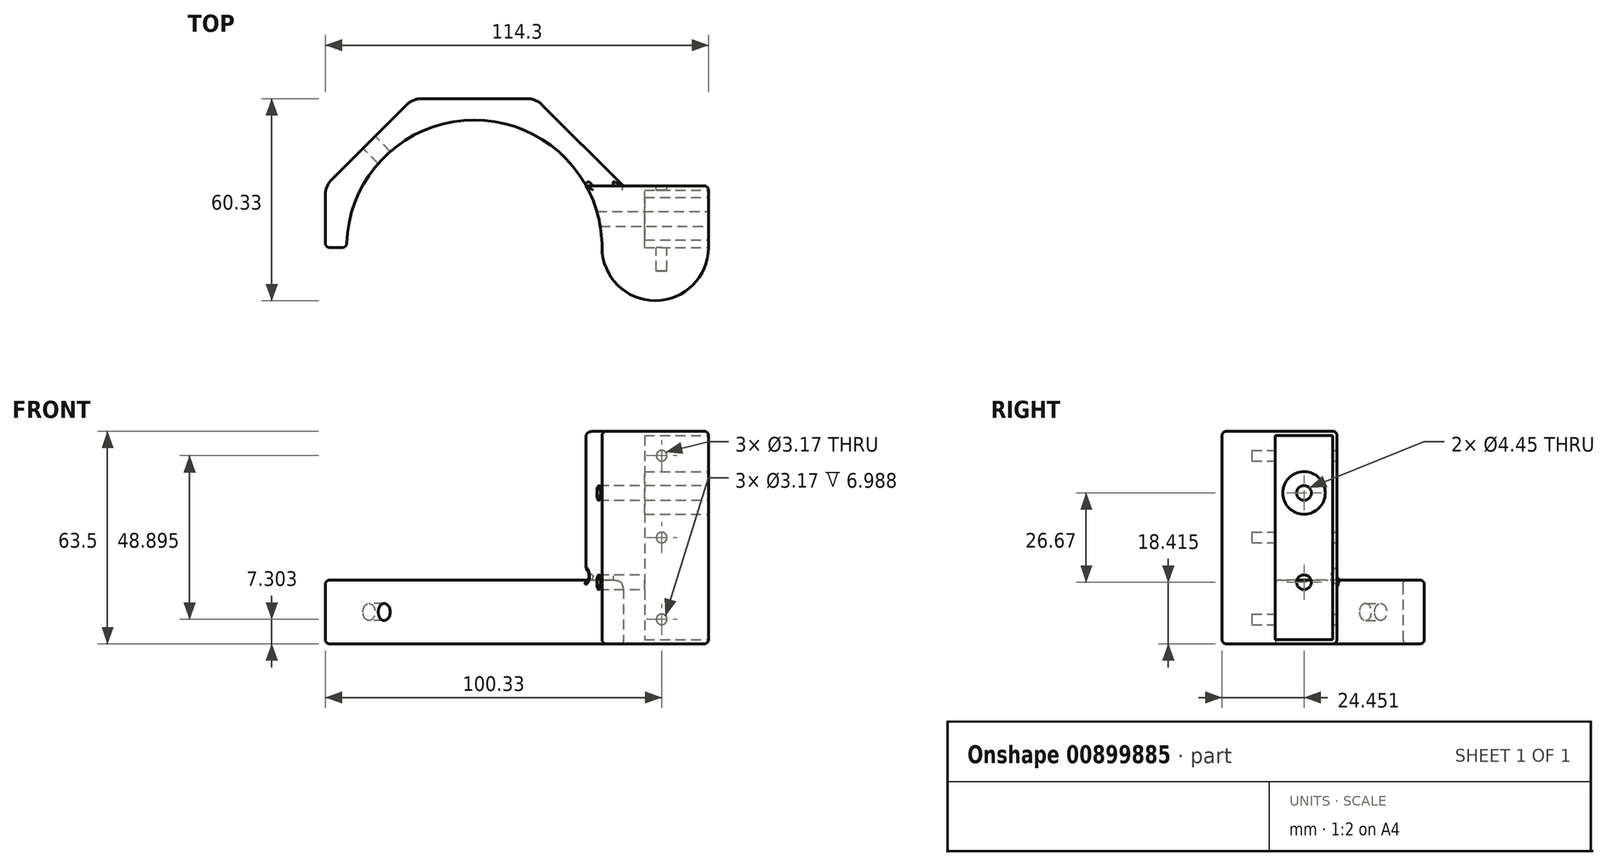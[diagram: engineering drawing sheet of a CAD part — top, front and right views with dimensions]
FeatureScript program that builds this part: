
annotation { "Feature Type Name" : "Feature", "Feature Type Description" : "" }
export const myFeature = defineFeature(function(context is Context, id is Id, definition is map)
    precondition{}
    {
        {
            var Q0;
            Q0=qCreatedBy(makeId("Top.planeOp"),FACE);
            var sketch = newSketch(context, id + "F0", { "sketchPlane" : qUnion([Q0])});
            skArc(sketch, "E0", {"start": v(38.1, 0) * mm, "mid": v(0, 38.1) * mm, "end": v(-38.1, 0) * mm});
            skCircle(sketch, "E1.cCircle", {"center": v(0, 0) * mm, "radius": 44.45 * mm, "construction": true});
            skLineSegment(sketch, "E1.0", {"start": v(44.45, 18.41) * mm, "end": v(44.45, 0) * mm});
            skLineSegment(sketch, "E1.4", {"start": v(-44.45, 0) * mm, "end": v(-44.45, 18.41) * mm});
            skLineSegment(sketch, "E1.5", {"start": v(-44.45, 18.41) * mm, "end": v(-18.41, 44.45) * mm});
            skLineSegment(sketch, "E1.6", {"start": v(-18.41, 44.45) * mm, "end": v(18.41, 44.45) * mm});
            skLineSegment(sketch, "E1.7", {"start": v(18.41, 44.45) * mm, "end": v(44.45, 18.41) * mm});
            skPoint(sketch, "E1.0.midPoint", {"position": v(44.45, 0) * mm});
            skLineSegment(sketch, "E2", {"start": v(-44.45, 0) * mm, "end": v(-38.1, 0) * mm});
            skPoint(sketch, "E3.orphan", {"position": v(-44.45, -18.41) * mm});
            skPoint(sketch, "E4.orphan", {"position": v(44.45, -18.41) * mm});
            skLineSegment(sketch, "E5.trimOffspring", {"start": v(38.1, 0) * mm, "end": v(44.45, 0) * mm});
            skLineSegment(sketch, "E6", {"start": v(44.45, 0) * mm, "end": v(69.85, 0) * mm});
            skLineSegment(sketch, "E7", {"start": v(69.85, 0) * mm, "end": v(69.85, 18.41) * mm});
            skLineSegment(sketch, "E8", {"start": v(69.85, 18.41) * mm, "end": v(44.45, 18.41) * mm});
            skArc(sketch, "E9", {"start": v(38.1, 0) * mm, "mid": v(53.98, -15.88) * mm, "end": v(69.85, 0) * mm});
            skLineSegment(sketch, "E10", {"start": v(44.45, 18.41) * mm, "end": v(33.36, 18.41) * mm});
            skSolve(sketch);
        }
        {
            var Q0;
            Q0=makeQuery(id+"F0.imprint","IMPRINT",FACE,{"disambiguationData":[TD([[makeQuery(id+"F0.imprint","IMPRINT",EDGE,{"derivedFrom":sQuery(id+"F0.wireOp",EDGE,"E1.0")}),1.0]])]});
            var Q1;
            Q1=makeQuery(id+"F0.imprint","IMPRINT",FACE,{"disambiguationData":[TD([[makeQuery(id+"F0.imprint","IMPRINT",EDGE,{"derivedFrom":sQuery(id+"F0.wireOp",EDGE,"E5.trimOffspring")}),-1.0]])]});
            var Q2;
            Q2=makeQuery(id+"F0.imprint","IMPRINT",FACE,{"disambiguationData":[TD([[makeQuery(id+"F0.imprint","IMPRINT",EDGE,{"derivedFrom":sQuery(id+"F0.wireOp",EDGE,"E1.0")}),-1.0]])]});
            extrude(context, id + "F1", {"entities" : qUnion([Q0, Q1, Q2]), "depth" : 63.5 * mm, "offsetDistance" : 25.4 * mm});
        }
        {
            var Q0;
            Q0=makeQuery(id+"F0.imprint","IMPRINT",FACE,{"disambiguationData":[TD([[makeQuery(id+"F0.imprint","IMPRINT",EDGE,{"derivedFrom":sQuery(id+"F0.wireOp",EDGE,"E1.4")}),-1.0]])]});
            extrude(context, id + "F2", {"entities" : qUnion([Q0]), "operationType" : NewBodyOperationType.ADD, "depth" : 19.05 * mm, "offsetDistance" : 25.4 * mm});
        }
        {
            var Q0;
            Q0=makeQuery(id+"F2.opExtrude","SWEPT_EDGE",EDGE,{"disambiguationData":[OSD([sQuery(id+"F0.wireOp",EDGE,"E1.0"),sQuery(id+"F0.wireOp",EDGE,"E1.7"),sQuery(id+"F0.wireOp",EDGE,"E8"),sQuery(id+"F0.wireOp",EDGE,"E10")])]});
            var Q1;
            Q1=makeQuery(id+"F2.opExtrude","SWEPT_EDGE",EDGE,{"disambiguationData":[OSD([sQuery(id+"F0.wireOp",EDGE,"E1.6"),sQuery(id+"F0.wireOp",EDGE,"E1.7")])]});
            var Q2;
            Q2=makeQuery(id+"F2.opExtrude","SWEPT_EDGE",EDGE,{"disambiguationData":[OSD([sQuery(id+"F0.wireOp",EDGE,"E1.5"),sQuery(id+"F0.wireOp",EDGE,"E1.6")])]});
            var Q3;
            Q3=makeQuery(id+"F2.opExtrude","SWEPT_EDGE",EDGE,{"disambiguationData":[OSD([sQuery(id+"F0.wireOp",EDGE,"E1.4"),sQuery(id+"F0.wireOp",EDGE,"E1.5")])]});
            var Q4;
            Q4=makeQuery(id+"F2.opExtrude","CAP_EDGE",EDGE,{"disambiguationData":[OSD([sQuery(id+"F0.wireOp",EDGE,"E10")])],"isStart":false});
            fillet(context, id + "F3", {"entities" : qUnion([Q0, Q1, Q2, Q3, Q4]), "radius" : 6.35 * mm, "tangentPropagation" : true, "allowEdgeOverflow" : false});
        }
        {
            var Q0;
            Q0=makeQuery(id+"F1.opExtrude","SWEPT_EDGE",EDGE,{"disambiguationData":[OSD([sQuery(id+"F0.wireOp",EDGE,"E7"),sQuery(id+"F0.wireOp",EDGE,"E8")])]});
            var Q1;
            {var subQ0=sQuery(id+"F0.wireOp",EDGE,"E10");var subQ1=sQuery(id+"F0.wireOp",EDGE,"E0");Q1=makeQuery(id+"F2.boolean.opBoolean","MERGE",FACE,{"derivedFrom":[makeQuery(id+"F1.opExtrude","CAP_FACE",FACE,{"disambiguationData":[OSD([subQ1,sQuery(id+"F0.wireOp",EDGE,"E7"),sQuery(id+"F0.wireOp",EDGE,"E8"),sQuery(id+"F0.wireOp",EDGE,"E9"),subQ0])],"isStart":true}),makeQuery(id+"F2.opExtrude","CAP_FACE",FACE,{"disambiguationData":[OSD([subQ1,sQuery(id+"F0.wireOp",EDGE,"E1.4"),sQuery(id+"F0.wireOp",EDGE,"E1.5"),sQuery(id+"F0.wireOp",EDGE,"E1.6"),sQuery(id+"F0.wireOp",EDGE,"E1.7"),sQuery(id+"F0.wireOp",EDGE,"E2"),subQ0])],"isStart":true})]});}
            var Q2;
            Q2=makeQuery(id+"F2.opExtrude","SWEPT_FACE",FACE,{"disambiguationData":[OSD([sQuery(id+"F0.wireOp",EDGE,"E2")])]});
            var Q3;
            Q3=makeQuery(id+"F2.opExtrude","CAP_FACE",FACE,{"disambiguationData":[OSD([sQuery(id+"F0.wireOp",EDGE,"E0"),sQuery(id+"F0.wireOp",EDGE,"E1.4"),sQuery(id+"F0.wireOp",EDGE,"E1.5"),sQuery(id+"F0.wireOp",EDGE,"E1.6"),sQuery(id+"F0.wireOp",EDGE,"E1.7"),sQuery(id+"F0.wireOp",EDGE,"E2"),sQuery(id+"F0.wireOp",EDGE,"E10")])],"isStart":false});
            var Q4;
            Q4=makeQuery(id+"F1.opExtrude","CAP_FACE",FACE,{"disambiguationData":[OSD([sQuery(id+"F0.wireOp",EDGE,"E0"),sQuery(id+"F0.wireOp",EDGE,"E7"),sQuery(id+"F0.wireOp",EDGE,"E8"),sQuery(id+"F0.wireOp",EDGE,"E9"),sQuery(id+"F0.wireOp",EDGE,"E10")])],"isStart":false});
            fillet(context, id + "F4", {"entities" : qUnion([Q0, Q1, Q2, Q3, Q4]), "radius" : 1.27 * mm, "tangentPropagation" : true, "allowEdgeOverflow" : false});
        }
        {
            var Q0;
            Q0=makeQuery(id+"F2.opExtrude","SWEPT_FACE",FACE,{"disambiguationData":[OSD([sQuery(id+"F0.wireOp",EDGE,"E1.5")])]});
            var sketch = newSketch(context, id + "F5", { "sketchPlane" : qUnion([Q0])});
            skLineSegment(sketch, "E11", {"start": v(15.78, 1.27) * mm, "end": v(-15.78, 17.78) * mm});
            skCircle(sketch, "E12", {"center": v(0, 9.53) * mm, "radius": 2.54 * mm});
            skSolve(sketch);
        }
        {
            var Q0;
            {var subQ0=sQuery(id+"F5.wireOp",EDGE,"E12");var subQ1=sQuery(id+"F5.wireOp",EDGE,"E11");var subQ2=makeQuery(id+"F5.imprint","INTERSECT",VERTEX,{"disambiguationData":[OD(0.0)],"derivedFrom":[subQ1,subQ0]});Q0=makeQuery(id+"F5.imprint","IMPRINT",FACE,{"disambiguationData":[TD([[makeQuery(id+"F5.imprint","IMPRINT",EDGE,{"disambiguationData":[TD([[subQ2,-1.0]])],"derivedFrom":subQ1}),-1.0]])]});}
            var Q1;
            {var subQ0=sQuery(id+"F5.wireOp",EDGE,"E12");var subQ1=sQuery(id+"F5.wireOp",EDGE,"E11");var subQ2=makeQuery(id+"F5.imprint","INTERSECT",VERTEX,{"disambiguationData":[OD(0.0)],"derivedFrom":[subQ1,subQ0]});Q1=makeQuery(id+"F5.imprint","IMPRINT",FACE,{"disambiguationData":[TD([[makeQuery(id+"F5.imprint","IMPRINT",EDGE,{"disambiguationData":[TD([[subQ2,-1.0]])],"derivedFrom":subQ1}),1.0]])]});}
            extrude(context, id + "F6", {"entities" : qUnion([Q0, Q1]), "operationType" : NewBodyOperationType.REMOVE, "oppositeDirection" : true, "depth" : 25.4 * mm, "offsetDistance" : 25.4 * mm});
        }
        {
            var Q0;
            Q0=makeQuery(id+"F1.opExtrude","SWEPT_FACE",FACE,{"disambiguationData":[OSD([sQuery(id+"F0.wireOp",EDGE,"E8"),sQuery(id+"F0.wireOp",EDGE,"E10")])]});
            var sketch = newSketch(context, id + "F7", { "sketchPlane" : qUnion([Q0])});
            skLineSegment(sketch, "E13", {"start": v(-68.58, 56.2) * mm, "end": v(-68.58, 7.3) * mm});
            skLineSegment(sketch, "E14.0", {"start": v(-55.88, 56.2) * mm, "end": v(-55.88, 7.3) * mm});
            skCircle(sketch, "E15", {"center": v(-55.88, 56.2) * mm, "radius": 1.59 * mm});
            skCircle(sketch, "E16", {"center": v(-55.88, 31.75) * mm, "radius": 1.59 * mm});
            skCircle(sketch, "E17", {"center": v(-55.88, 7.3) * mm, "radius": 1.59 * mm});
            skSolve(sketch);
        }
        {
            var Q0;
            Q0=makeQuery(id+"F7.imprint","IMPRINT",FACE,{"disambiguationData":[TD([[makeQuery(id+"F7.imprint","IMPRINT",EDGE,{"derivedFrom":sQuery(id+"F7.wireOp",EDGE,"E15")}),1.0]])]});
            var Q1;
            {var subQ0=sQuery(id+"F7.wireOp",EDGE,"E16");var subQ1=sQuery(id+"F7.wireOp",EDGE,"E14.0");var subQ2=makeQuery(id+"F7.imprint","INTERSECT",VERTEX,{"disambiguationData":[OD(0.0)],"derivedFrom":[subQ1,subQ0]});Q1=makeQuery(id+"F7.imprint","IMPRINT",FACE,{"disambiguationData":[TD([[makeQuery(id+"F7.imprint","IMPRINT",EDGE,{"disambiguationData":[TD([[subQ2,1.0]])],"derivedFrom":subQ1}),1.0]])]});}
            var Q2;
            {var subQ0=sQuery(id+"F7.wireOp",EDGE,"E16");var subQ1=sQuery(id+"F7.wireOp",EDGE,"E14.0");var subQ2=makeQuery(id+"F7.imprint","INTERSECT",VERTEX,{"disambiguationData":[OD(0.0)],"derivedFrom":[subQ1,subQ0]});Q2=makeQuery(id+"F7.imprint","IMPRINT",FACE,{"disambiguationData":[TD([[makeQuery(id+"F7.imprint","IMPRINT",EDGE,{"disambiguationData":[TD([[subQ2,1.0]])],"derivedFrom":subQ1}),-1.0]])]});}
            var Q3;
            Q3=makeQuery(id+"F7.imprint","IMPRINT",FACE,{"disambiguationData":[TD([[makeQuery(id+"F7.imprint","IMPRINT",EDGE,{"derivedFrom":sQuery(id+"F7.wireOp",EDGE,"E17")}),1.0]])]});
            extrude(context, id + "F8", {"entities" : qUnion([Q0, Q1, Q2, Q3]), "operationType" : NewBodyOperationType.REMOVE, "oppositeDirection" : true, "depth" : 25.4 * mm, "offsetDistance" : 25.4 * mm});
        }
        {
            var Q0;
            Q0=makeQuery(id+"F1.opExtrude","SWEPT_FACE",FACE,{"disambiguationData":[OSD([sQuery(id+"F0.wireOp",EDGE,"E7")])]});
            var sketch = newSketch(context, id + "F9", { "sketchPlane" : qUnion([Q0])});
            skLineSegment(sketch, "E18", {"start": v(8.57, 62.23) * mm, "end": v(8.57, 1.27) * mm});
            skCircle(sketch, "E19", {"center": v(8.57, 45.09) * mm, "radius": 2.22 * mm});
            skCircle(sketch, "E20", {"center": v(8.57, 18.42) * mm, "radius": 2.22 * mm});
            skCircle(sketch, "E21", {"center": v(8.57, 45.09) * mm, "radius": 6.35 * mm});
            skCircle(sketch, "E22", {"center": v(8.57, 18.42) * mm, "radius": 6.35 * mm});
            skSolve(sketch);
        }
        {
            var Q0;
            {var subQ0=sQuery(id+"F9.wireOp",EDGE,"E19");var subQ1=sQuery(id+"F9.wireOp",EDGE,"E18");var subQ2=makeQuery(id+"F9.imprint","INTERSECT",VERTEX,{"disambiguationData":[OD(0.0)],"derivedFrom":[subQ1,subQ0]});Q0=makeQuery(id+"F9.imprint","IMPRINT",FACE,{"disambiguationData":[TD([[makeQuery(id+"F9.imprint","IMPRINT",EDGE,{"disambiguationData":[TD([[subQ2,-1.0]])],"derivedFrom":subQ1}),1.0]])]});}
            var Q1;
            {var subQ0=sQuery(id+"F9.wireOp",EDGE,"E19");var subQ1=sQuery(id+"F9.wireOp",EDGE,"E18");var subQ2=makeQuery(id+"F9.imprint","INTERSECT",VERTEX,{"disambiguationData":[OD(0.0)],"derivedFrom":[subQ1,subQ0]});Q1=makeQuery(id+"F9.imprint","IMPRINT",FACE,{"disambiguationData":[TD([[makeQuery(id+"F9.imprint","IMPRINT",EDGE,{"disambiguationData":[TD([[subQ2,-1.0]])],"derivedFrom":subQ1}),-1.0]])]});}
            var Q2;
            {var subQ0=sQuery(id+"F9.wireOp",EDGE,"E20");var subQ1=sQuery(id+"F9.wireOp",EDGE,"E18");var subQ2=makeQuery(id+"F9.imprint","INTERSECT",VERTEX,{"disambiguationData":[OD(0.0)],"derivedFrom":[subQ1,subQ0]});Q2=makeQuery(id+"F9.imprint","IMPRINT",FACE,{"disambiguationData":[TD([[makeQuery(id+"F9.imprint","IMPRINT",EDGE,{"disambiguationData":[TD([[subQ2,-1.0]])],"derivedFrom":subQ1}),1.0]])]});}
            var Q3;
            {var subQ0=sQuery(id+"F9.wireOp",EDGE,"E20");var subQ1=sQuery(id+"F9.wireOp",EDGE,"E18");var subQ2=makeQuery(id+"F9.imprint","INTERSECT",VERTEX,{"disambiguationData":[OD(0.0)],"derivedFrom":[subQ1,subQ0]});Q3=makeQuery(id+"F9.imprint","IMPRINT",FACE,{"disambiguationData":[TD([[makeQuery(id+"F9.imprint","IMPRINT",EDGE,{"disambiguationData":[TD([[subQ2,-1.0]])],"derivedFrom":subQ1}),-1.0]])]});}
            extrude(context, id + "F10", {"entities" : qUnion([Q0, Q1, Q2, Q3]), "operationType" : NewBodyOperationType.REMOVE, "oppositeDirection" : true, "depth" : 76.2 * mm, "offsetDistance" : 25.4 * mm});
        }
        {
            var Q0;
            {var subQ0=sQuery(id+"F9.wireOp",EDGE,"E21");var subQ1=sQuery(id+"F9.wireOp",EDGE,"E18");var subQ2=makeQuery(id+"F9.imprint","INTERSECT",VERTEX,{"disambiguationData":[OD(0.0)],"derivedFrom":[subQ1,subQ0]});Q0=makeQuery(id+"F9.imprint","IMPRINT",FACE,{"disambiguationData":[TD([[makeQuery(id+"F9.imprint","IMPRINT",EDGE,{"disambiguationData":[TD([[subQ2,-1.0]])],"derivedFrom":subQ1}),1.0]])]});}
            var Q1;
            {var subQ0=sQuery(id+"F9.wireOp",EDGE,"E21");var subQ1=sQuery(id+"F9.wireOp",EDGE,"E18");var subQ2=makeQuery(id+"F9.imprint","INTERSECT",VERTEX,{"disambiguationData":[OD(0.0)],"derivedFrom":[subQ1,subQ0]});Q1=makeQuery(id+"F9.imprint","IMPRINT",FACE,{"disambiguationData":[TD([[makeQuery(id+"F9.imprint","IMPRINT",EDGE,{"disambiguationData":[TD([[subQ2,-1.0]])],"derivedFrom":subQ1}),-1.0]])]});}
            var Q2;
            {var subQ0=sQuery(id+"F9.wireOp",EDGE,"E22");var subQ1=sQuery(id+"F9.wireOp",EDGE,"E18");var subQ2=makeQuery(id+"F9.imprint","INTERSECT",VERTEX,{"disambiguationData":[OD(0.0)],"derivedFrom":[subQ1,subQ0]});Q2=makeQuery(id+"F9.imprint","IMPRINT",FACE,{"disambiguationData":[TD([[makeQuery(id+"F9.imprint","IMPRINT",EDGE,{"disambiguationData":[TD([[subQ2,-1.0]])],"derivedFrom":subQ1}),1.0]])]});}
            var Q3;
            {var subQ0=sQuery(id+"F9.wireOp",EDGE,"E22");var subQ1=sQuery(id+"F9.wireOp",EDGE,"E18");var subQ2=makeQuery(id+"F9.imprint","INTERSECT",VERTEX,{"disambiguationData":[OD(0.0)],"derivedFrom":[subQ1,subQ0]});Q3=makeQuery(id+"F9.imprint","IMPRINT",FACE,{"disambiguationData":[TD([[makeQuery(id+"F9.imprint","IMPRINT",EDGE,{"disambiguationData":[TD([[subQ2,-1.0]])],"derivedFrom":subQ1}),-1.0]])]});}
            extrude(context, id + "F11", {"entities" : qUnion([Q0, Q1, Q2, Q3]), "operationType" : NewBodyOperationType.REMOVE, "oppositeDirection" : true, "depth" : 19.05 * mm, "offsetDistance" : 25.4 * mm});
        }
    });
